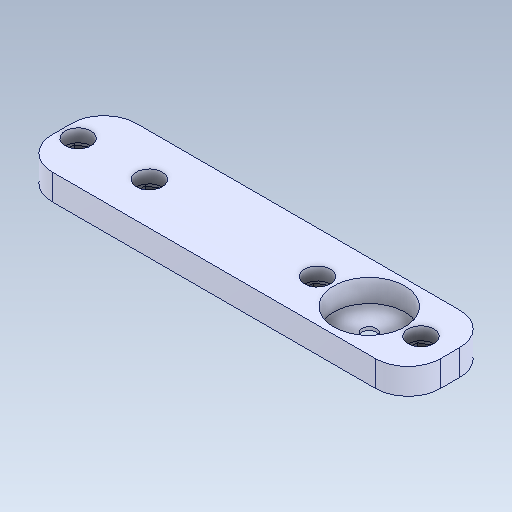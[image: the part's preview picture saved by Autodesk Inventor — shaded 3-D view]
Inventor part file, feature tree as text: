
AUTODESK INVENTOR PART (.ipt)
format: ipt  version: 2021 (Build 250183000, 183)  size: 139,264 bytes
history: mixed  units: in
note: dims shown in document units (in); Inventor stores cm internally (conversion verified against a paired STEP export)
features: fillet x1, imported_body x1
ambient origin geometry x8: Origin, YZ Plane, XZ Plane, XY Plane, X Axis, Y Axis, Z Axis, Center Point
bodies: Solid1 (imported_parasolid)
feature tree (2):
  fillet  "Fillet1"  [1 undecoded]
  imported_body  NMx_Import_Brep_tag  [imported B-rep: ~53 faces, bbox_mm=[120.0, 8.0, 26.0]]
note: 1 required parameter value undecoded (feature->parameter linkage not recoverable at this tier; creation-order binding heuristic only, values carry confidence <= 0.55)
